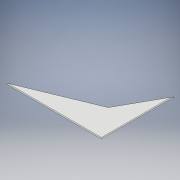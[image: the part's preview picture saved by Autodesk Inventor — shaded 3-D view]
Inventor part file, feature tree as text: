
AUTODESK INVENTOR PART (.ipt)
format: ipt  version: 2017 (Build 210142000, 142)  size: 105,984 bytes
history: native  units: in
note: dims shown in document units (in); Inventor stores cm internally (conversion verified against a paired STEP export)
features: chamfer x4, extrude x1, sketch x1
ambient origin geometry x8: Origin, YZ Plane, XZ Plane, XY Plane, X Axis, Y Axis, Z Axis, Center Point
bodies: Solid1 (feature_tree)
feature tree (6):
  extrude  "Extrusion1"  Depth=0.05in
  chamfer  "Chamfer1"  Distance=0.05in
  chamfer  "Chamfer2"  Distance=0.025in Angle=45.0deg
  chamfer  "Chamfer3"  Distance=0.025in Angle=45.0deg
  chamfer  "Chamfer4"  Distance=0.025in Angle=45.0deg
  sketch  "Sketch1"  dims[d0=4.0in d1=3.0in d3=0.05in d4=0.0in d5=0.025in d6=0.125in d7=45.0deg d8=0.025in d9=0.125in d10=45.0deg d11=0.025in d12=0.125in d13=45.0deg d14=0.025in d15=0.125in d16=45.0deg]
